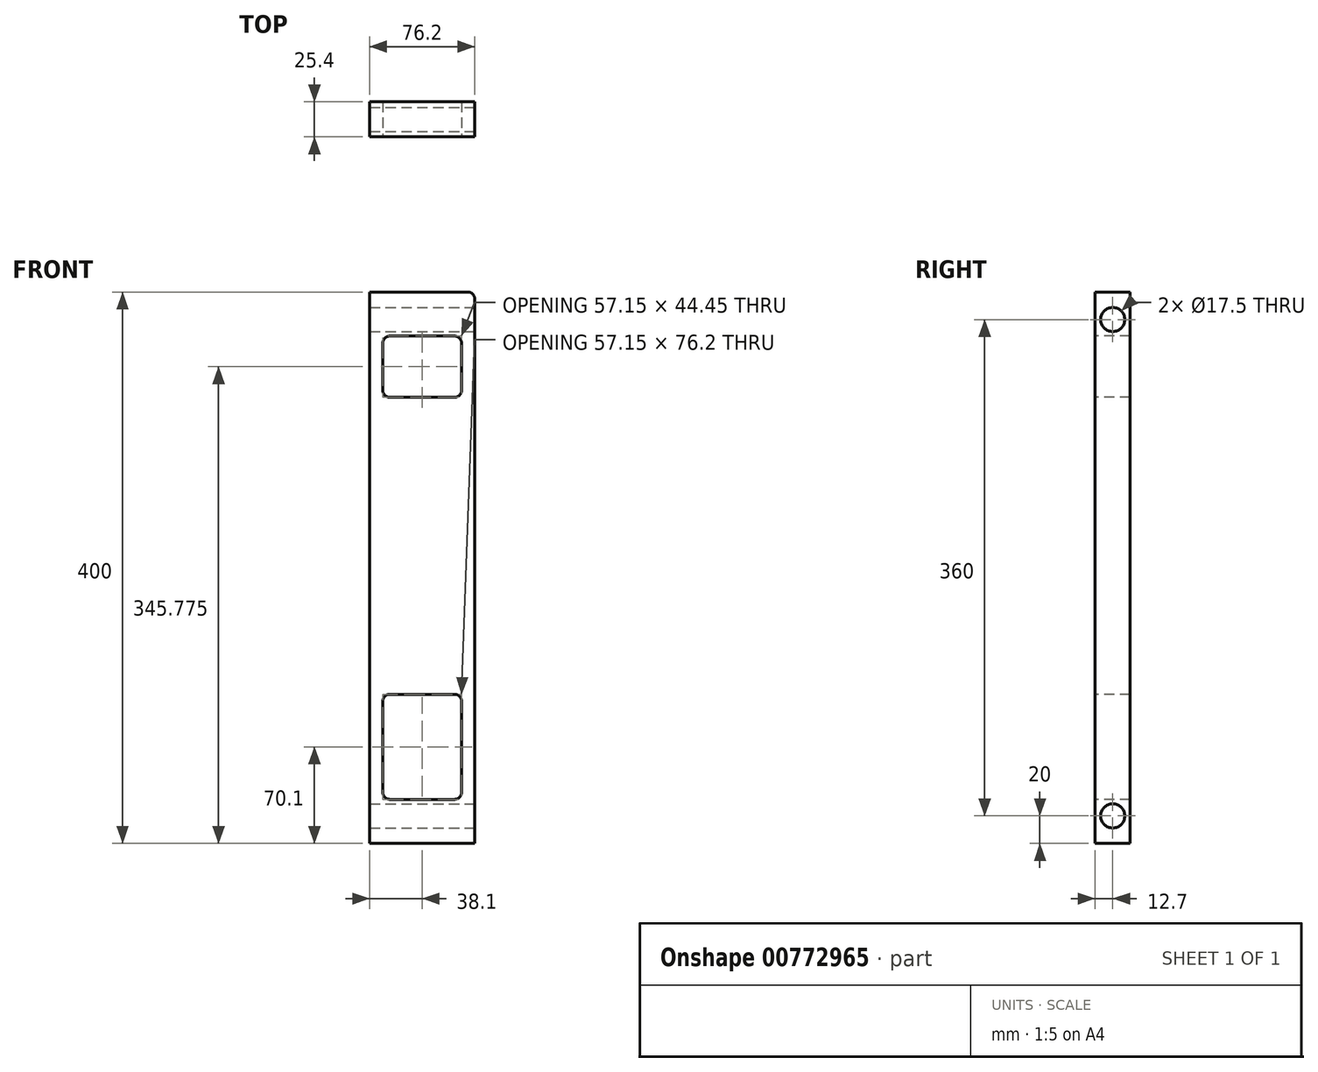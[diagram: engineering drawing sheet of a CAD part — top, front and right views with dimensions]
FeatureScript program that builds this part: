
annotation { "Feature Type Name" : "Feature", "Feature Type Description" : "" }
export const myFeature = defineFeature(function(context is Context, id is Id, definition is map)
    precondition{}
    {
        {
            var Q0;
            Q0=qCreatedBy(makeId("Front.planeOp"),FACE);
            var sketch = newSketch(context, id + "F0", { "sketchPlane" : qUnion([Q0])});
            skLineSegment(sketch, "E0", {"start": v(0, 0) * mm, "end": v(0, 400) * mm});
            skLineSegment(sketch, "E1", {"start": v(0, 400) * mm, "end": v(76.2, 400) * mm});
            skLineSegment(sketch, "E2", {"start": v(0, 0) * mm, "end": v(76.2, 0) * mm});
            skLineSegment(sketch, "E3", {"start": v(76.2, 0) * mm, "end": v(76.2, 400) * mm});
            skLineSegment(sketch, "E4", {"start": v(76.2, 400) * mm, "end": v(76.2, 400) * mm});
            skSolve(sketch);
        }
        {
            var Q0;
            Q0=makeQuery(id+"F0.imprint","IMPRINT",FACE,{"disambiguationData":[TD([[makeQuery(id+"F0.imprint","IMPRINT",EDGE,{"derivedFrom":sQuery(id+"F0.wireOp",EDGE,"E0")}),-1.0]])]});
            extrude(context, id + "F1", {"entities" : qUnion([Q0]), "depth" : 25.4 * mm, "offsetDistance" : 25.4 * mm});
        }
        {
            var Q0;
            Q0=makeQuery(id+"F1.opExtrude","SWEPT_FACE",FACE,{"disambiguationData":[OSD([sQuery(id+"F0.wireOp",EDGE,"E3")])]});
            var sketch = newSketch(context, id + "F2", { "sketchPlane" : qUnion([Q0])});
            skLineSegment(sketch, "E5", {"start": v(-12.7, 0) * mm, "end": v(-12.7, 20) * mm});
            skLineSegment(sketch, "E6", {"start": v(-12.7, 20) * mm, "end": v(-12.7, 380) * mm});
            skSolve(sketch);
        }
        {
            var Q0;
            Q0=sQuery(id+"F2.wireOp",VERTEX,"E6.end");
            var Q1;
            Q1=sQuery(id+"F2.wireOp",VERTEX,"E5.end");
            var Q2;
            Q2=makeQuery(id+"F1.opExtrude","SWEPT_BODY",BODY,{"disambiguationData":[OSD([sQuery(id+"F0.wireOp",EDGE,"E0"),sQuery(id+"F0.wireOp",EDGE,"E1"),sQuery(id+"F0.wireOp",EDGE,"E2"),sQuery(id+"F0.wireOp",EDGE,"E3")])]});
            hole(context, id + "F3", {"style" : HoleStyle.SIMPLE, "endStyle" : HoleEndStyle.THROUGH, "standardTappedOrClearance" : lookupTablePath({ "standard" : "ISO", "fit" : "Normal", "size" : "M16", "type" : "Clearance" }), "standardBlindInLast" : lookupTablePath({ "fit" : "Standard", "standard" : "ISO", "size" : "M16", "type" : "Clearance" }), "holeDiameter" : 17.5 * mm, "majorDiameter" : 6.35 * mm, "tappedDepth" : 19.4 * mm, "tapClearance" : 3, "locations" : qUnion([Q0, Q1]), "scope" : qUnion([Q2])});
        }
        {
            var Q0;
            Q0=makeQuery(id+"F1.opExtrude","CAP_FACE",FACE,{"disambiguationData":[OSD([sQuery(id+"F0.wireOp",EDGE,"E0"),sQuery(id+"F0.wireOp",EDGE,"E1"),sQuery(id+"F0.wireOp",EDGE,"E2"),sQuery(id+"F0.wireOp",EDGE,"E3")])],"isStart":false});
            var sketch = newSketch(context, id + "F4", { "sketchPlane" : qUnion([Q0])});
            skLineSegment(sketch, "E7", {"start": v(0, 0) * mm, "end": v(9.53, 0) * mm});
            skLineSegment(sketch, "E8", {"start": v(76.2, 0) * mm, "end": v(66.67, 0) * mm});
            skLineSegment(sketch, "E9", {"start": v(66.67, 0) * mm, "end": v(66.67, 32) * mm});
            skLineSegment(sketch, "E10", {"start": v(9.53, 0) * mm, "end": v(9.53, 32) * mm});
            skLineSegment(sketch, "E11.bottom", {"start": v(9.52, 32) * mm, "end": v(66.68, 32) * mm});
            skLineSegment(sketch, "E11.top", {"start": v(9.52, 108.2) * mm, "end": v(66.67, 108.2) * mm});
            skLineSegment(sketch, "E11.left", {"start": v(9.53, 32) * mm, "end": v(9.53, 108.2) * mm});
            skLineSegment(sketch, "E11.right", {"start": v(66.68, 32) * mm, "end": v(66.67, 108.2) * mm});
            skLineSegment(sketch, "E12", {"start": v(0, 200) * mm, "end": v(22.17, 200) * mm});
            skLineSegment(sketch, "E13.MirrorCS", {"start": v(9.52, 368) * mm, "end": v(66.68, 368) * mm});
            skLineSegment(sketch, "E14.top", {"start": v(9.52, 323.55) * mm, "end": v(66.68, 323.55) * mm});
            skLineSegment(sketch, "E14.left", {"start": v(9.52, 368) * mm, "end": v(9.52, 323.55) * mm});
            skLineSegment(sketch, "E14.right", {"start": v(66.68, 368) * mm, "end": v(66.68, 323.55) * mm});
            skSolve(sketch);
        }
        {
            var Q0;
            Q0=makeQuery(id+"F4.imprint","IMPRINT",FACE,{"disambiguationData":[TD([[makeQuery(id+"F4.imprint","IMPRINT",EDGE,{"derivedFrom":sQuery(id+"F4.wireOp",EDGE,"E11.bottom")}),1.0]])]});
            var Q1;
            Q1=makeQuery(id+"F4.imprint","IMPRINT",FACE,{"disambiguationData":[TD([[makeQuery(id+"F4.imprint","IMPRINT",EDGE,{"derivedFrom":sQuery(id+"F4.wireOp",EDGE,"E13.MirrorCS")}),-1.0]])]});
            extrude(context, id + "F5", {"entities" : qUnion([Q0, Q1]), "operationType" : NewBodyOperationType.REMOVE, "endBound" : BoundingType.THROUGH_ALL, "oppositeDirection" : true, "depth" : 25.4 * mm, "offsetDistance" : 25.4 * mm});
        }
        {
            var Q0;
            Q0=makeQuery(id+"F5.boolean.opBoolean","COPY",EDGE,{"derivedFrom":makeQuery(id+"F5.opExtrude","SWEPT_EDGE",EDGE,{"disambiguationData":[OSD([sQuery(id+"F4.wireOp",EDGE,"E11.top"),sQuery(id+"F4.wireOp",EDGE,"E11.left")])]})});
            var Q1;
            Q1=makeQuery(id+"F5.boolean.opBoolean","COPY",EDGE,{"derivedFrom":makeQuery(id+"F5.opExtrude","SWEPT_EDGE",EDGE,{"disambiguationData":[OSD([sQuery(id+"F4.wireOp",EDGE,"E11.top"),sQuery(id+"F4.wireOp",EDGE,"E11.right")])]})});
            var Q2;
            Q2=makeQuery(id+"F5.boolean.opBoolean","COPY",EDGE,{"derivedFrom":makeQuery(id+"F5.opExtrude","SWEPT_EDGE",EDGE,{"disambiguationData":[OSD([sQuery(id+"F4.wireOp",EDGE,"E9"),sQuery(id+"F4.wireOp",EDGE,"E11.bottom"),sQuery(id+"F4.wireOp",EDGE,"E11.right")])]})});
            var Q3;
            Q3=makeQuery(id+"F5.boolean.opBoolean","COPY",EDGE,{"derivedFrom":makeQuery(id+"F5.opExtrude","SWEPT_EDGE",EDGE,{"disambiguationData":[OSD([sQuery(id+"F4.wireOp",EDGE,"E10"),sQuery(id+"F4.wireOp",EDGE,"E11.bottom"),sQuery(id+"F4.wireOp",EDGE,"E11.left")])]})});
            var Q4;
            Q4=makeQuery(id+"F5.boolean.opBoolean","COPY",EDGE,{"derivedFrom":makeQuery(id+"F5.opExtrude","SWEPT_EDGE",EDGE,{"disambiguationData":[OSD([sQuery(id+"F4.wireOp",EDGE,"E14.top"),sQuery(id+"F4.wireOp",EDGE,"E14.left")])]})});
            var Q5;
            Q5=makeQuery(id+"F5.boolean.opBoolean","COPY",EDGE,{"derivedFrom":makeQuery(id+"F5.opExtrude","SWEPT_EDGE",EDGE,{"disambiguationData":[OSD([sQuery(id+"F4.wireOp",EDGE,"E14.top"),sQuery(id+"F4.wireOp",EDGE,"E14.right")])]})});
            var Q6;
            Q6=makeQuery(id+"F5.boolean.opBoolean","COPY",EDGE,{"derivedFrom":makeQuery(id+"F5.opExtrude","SWEPT_EDGE",EDGE,{"disambiguationData":[OSD([sQuery(id+"F4.wireOp",EDGE,"E13.MirrorCS"),sQuery(id+"F4.wireOp",EDGE,"E14.left")])]})});
            var Q7;
            Q7=makeQuery(id+"F5.boolean.opBoolean","COPY",EDGE,{"derivedFrom":makeQuery(id+"F5.opExtrude","SWEPT_EDGE",EDGE,{"disambiguationData":[OSD([sQuery(id+"F4.wireOp",EDGE,"E13.MirrorCS"),sQuery(id+"F4.wireOp",EDGE,"E14.right")])]})});
            fillet(context, id + "F6", {"entities" : qUnion([Q0, Q1, Q2, Q3, Q4, Q5, Q6, Q7]), "radius" : 5.08 * mm, "tangentPropagation" : true, "allowEdgeOverflow" : false});
        }
        {
            var Q0;
            Q0=makeQuery(id+"F1.opExtrude","SWEPT_EDGE",EDGE,{"disambiguationData":[OSD([sQuery(id+"F0.wireOp",EDGE,"E1"),sQuery(id+"F0.wireOp",EDGE,"E3")])]});
            fillet(context, id + "F7", {"entities" : qUnion([Q0]), "radius" : 5.08 * mm, "tangentPropagation" : true, "allowEdgeOverflow" : false});
        }
    });
